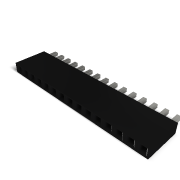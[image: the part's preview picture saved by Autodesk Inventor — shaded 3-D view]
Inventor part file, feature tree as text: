
AUTODESK INVENTOR PART (.ipt)
format: ipt  version: 2020 (Build 240168000, 168)  size: 341,504 bytes
history: native  units: in
note: dims shown in document units (in); Inventor stores cm internally (conversion verified against a paired STEP export)
features: extrude x3, sketch x3, chamfer x2, other x2, pattern_linear x1
ambient origin geometry x8: Origin, YZ Plane, XZ Plane, XY Plane, X Axis, Y Axis, Z Axis, Center Point
bodies: Solid1 (feature_tree)
feature tree (11):
  extrude  "Extrusion1"  Depth=0.1in
  extrude  "Extrusion2"  Depth=0.045in
  chamfer  "Chamfer1"  Distance=0.25in
  extrude  "Extrusion3"  Depth=0.035in
  chamfer  "Chamfer2"  Distance=0.13in
  pattern_linear  "Rectangular Pattern1"  Spacing1=0.015in  [1 undecoded]
  other  "Work Axis1"
  sketch  "Sketch1"  dims[d0=0.1in d1=0.1in]
  sketch  "Sketch2"  dims[d2=0.33in d3=0.0in d4=0.045in d5=0.25in d6=0.0in]
  sketch  "Sketch3"  dims[d7=0.015in d8=0.125in d9=45.0deg d10=0.035in d11=0.13in d12=0.0in d13=0.015in d14=0.125in d15=45.0deg d16=5.9055in d18=0.1in]
  other  "Work Point1"
note: 1 required parameter value undecoded (feature->parameter linkage not recoverable at this tier; creation-order binding heuristic only, values carry confidence <= 0.55)
